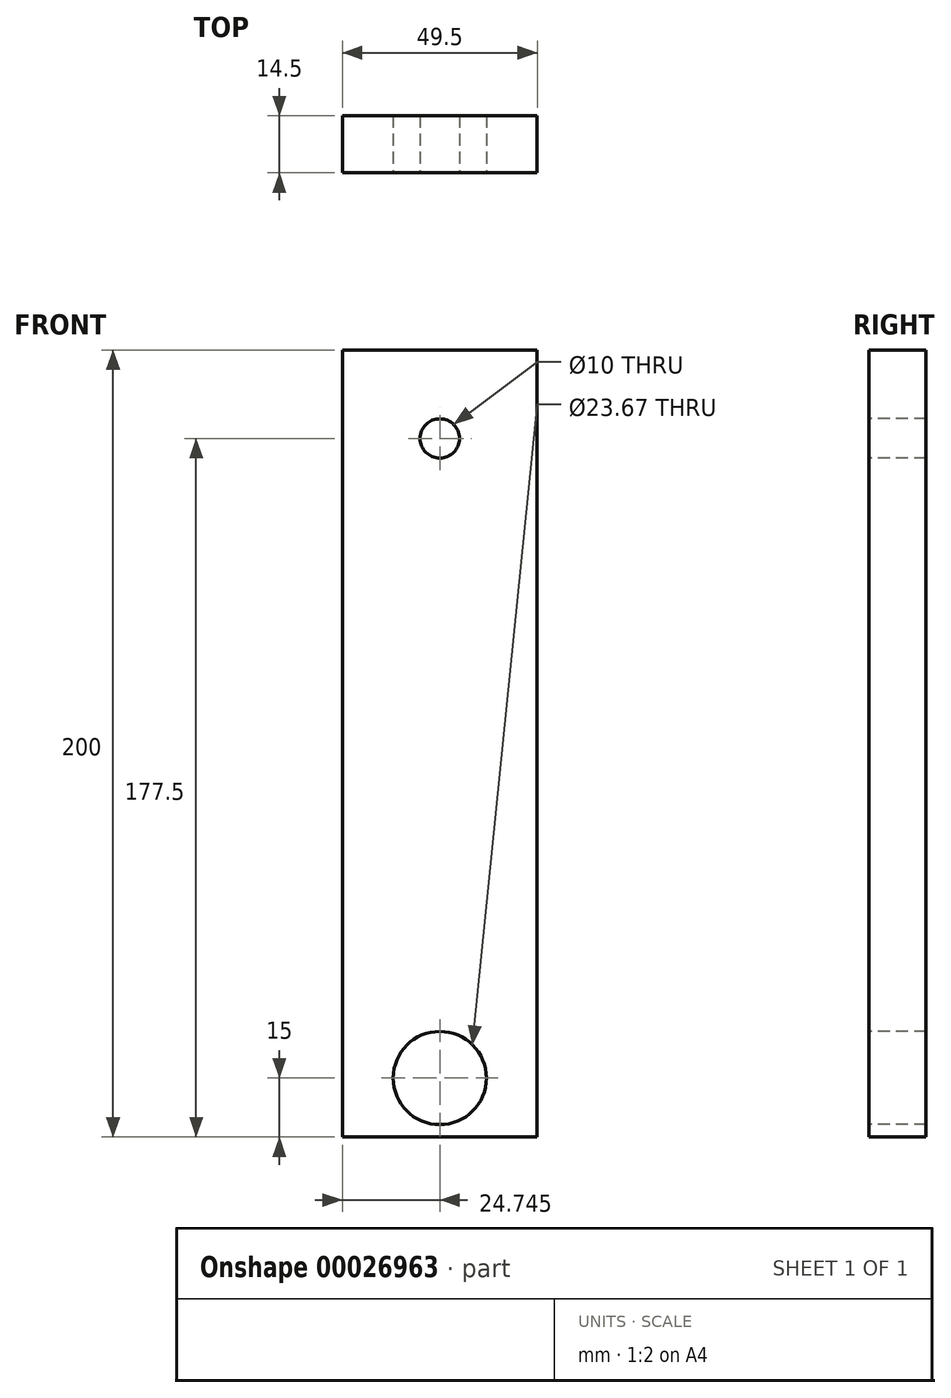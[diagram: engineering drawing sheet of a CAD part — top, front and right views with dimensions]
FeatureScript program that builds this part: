
annotation { "Feature Type Name" : "Feature", "Feature Type Description" : "" }
export const myFeature = defineFeature(function(context is Context, id is Id, definition is map)
    precondition{}
    {
        {
            var Q0;
            Q0=qCreatedBy(makeId("Top.planeOp"),FACE);
            var sketch = newSketch(context, id + "F0", { "sketchPlane" : qUnion([Q0])});
            skLineSegment(sketch, "E0.bottom", {"start": v(-22.26, 1.87) * mm, "end": v(27.24, 1.87) * mm});
            skLineSegment(sketch, "E0.top", {"start": v(-22.26, -12.63) * mm, "end": v(27.24, -12.63) * mm});
            skLineSegment(sketch, "E0.left", {"start": v(-22.26, 1.87) * mm, "end": v(-22.26, -12.63) * mm});
            skLineSegment(sketch, "E0.right", {"start": v(27.24, 1.87) * mm, "end": v(27.24, -12.63) * mm});
            skSolve(sketch);
        }
        {
            var Q0;
            Q0=makeQuery(id+"F0.imprint","IMPRINT",FACE,{"disambiguationData":[TD([[makeQuery(id+"F0.imprint","IMPRINT",EDGE,{"derivedFrom":sQuery(id+"F0.wireOp",EDGE,"E0.bottom")}),-1.0]])]});
            extrude(context, id + "F1", {"entities" : qUnion([Q0]), "depth" : 200 * mm});
        }
        {
            var Q0;
            Q0=makeQuery(id+"F1.opExtrude","SWEPT_FACE",FACE,{"disambiguationData":[OSD([sQuery(id+"F0.wireOp",EDGE,"E0.top")])]});
            var sketch = newSketch(context, id + "F2", { "sketchPlane" : qUnion([Q0])});
            skCircle(sketch, "E1", {"center": v(2.49, 15) * mm, "radius": 11.84 * mm});
            skCircle(sketch, "E2", {"center": v(2.49, 177.5) * mm, "radius": 5 * mm});
            skSolve(sketch);
        }
        {
            var Q0;
            Q0=makeQuery(id+"F2.imprint","IMPRINT",FACE,{"disambiguationData":[TD([[makeQuery(id+"F2.imprint","IMPRINT",EDGE,{"derivedFrom":sQuery(id+"F2.wireOp",EDGE,"E1")}),1.0]])]});
            var Q1;
            Q1=makeQuery(id+"F2.imprint","IMPRINT",FACE,{"disambiguationData":[TD([[makeQuery(id+"F2.imprint","IMPRINT",EDGE,{"derivedFrom":sQuery(id+"F2.wireOp",EDGE,"E2")}),1.0]])]});
            extrude(context, id + "F3", {"entities" : qUnion([Q0, Q1]), "operationType" : NewBodyOperationType.REMOVE, "endBound" : BoundingType.THROUGH_ALL, "oppositeDirection" : true, "depth" : 25 * mm});
        }
    });
